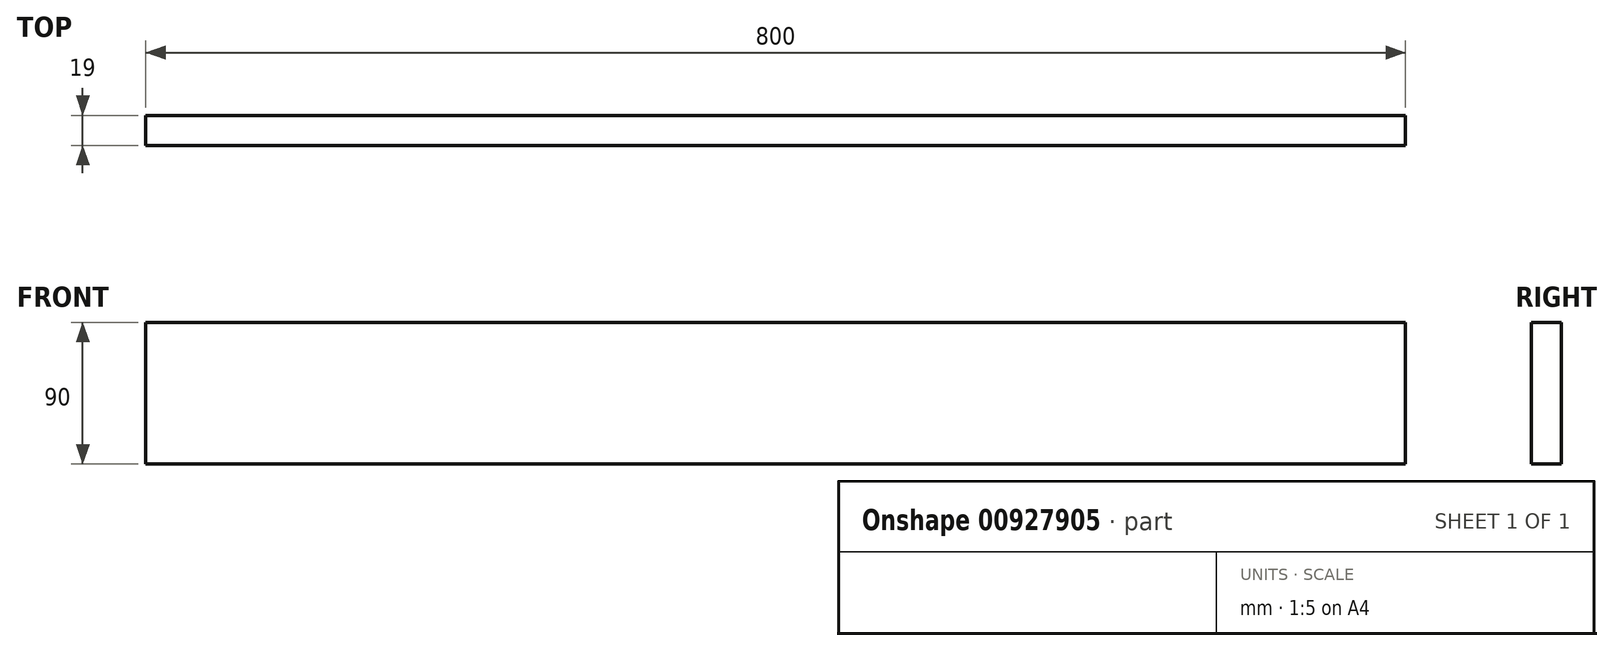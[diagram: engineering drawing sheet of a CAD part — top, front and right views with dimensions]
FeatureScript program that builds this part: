
annotation { "Feature Type Name" : "Feature", "Feature Type Description" : "" }
export const myFeature = defineFeature(function(context is Context, id is Id, definition is map)
    precondition{}
    {
        {
            var Q0;
            Q0=qCreatedBy(makeId("Front.planeOp"),FACE);
            var sketch = newSketch(context, id + "F0", { "sketchPlane" : qUnion([Q0])});
            skLineSegment(sketch, "E0.bottom", {"start": v(0, 0) * mm, "end": v(800, 0) * mm});
            skLineSegment(sketch, "E0.top", {"start": v(0, 90) * mm, "end": v(800, 90) * mm});
            skLineSegment(sketch, "E0.left", {"start": v(0, 0) * mm, "end": v(0, 90) * mm});
            skLineSegment(sketch, "E0.right", {"start": v(800, 0) * mm, "end": v(800, 90) * mm});
            skSolve(sketch);
        }
        {
            var Q0;
            Q0=qSketchRegion(id+"F0",true);
            extrude(context, id + "F1", {"entities" : qUnion([Q0]), "depth" : 19 * mm, "offsetDistance" : 25 * mm});
        }
    });
